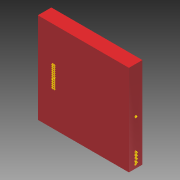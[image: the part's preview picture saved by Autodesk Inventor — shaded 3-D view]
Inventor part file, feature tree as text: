
AUTODESK INVENTOR PART (.ipt)
format: ipt  version: 2011 SP1 (Build 150282100, 282)  size: 317,440 bytes
history: native  units: in
note: dims shown in document units (in); Inventor stores cm internally (conversion verified against a paired STEP export)
features: sketch x14, extrude x4
ambient origin geometry x8: Origin, YZ Plane, XZ Plane, XY Plane, X Axis, Y Axis, Z Axis, Center Point
bodies: Solid1 (feature_tree)
feature tree (18):
  extrude  "Extrusion1"  Depth=3.37in
  extrude  "Extrusion2"  Depth=1.25in
  extrude  "Extrusion3"  Depth=0.5in
  extrude  "Extrusion4"  Depth=0.01in TaperAngle=0.0deg
  sketch  "Sketch5"  dims[d10=0.01in]
  sketch  "Sketch6"  dims[d11=5.1181in d13=0.0625in d14=0.3937in d16=1.0in]
  sketch  "Sketch7"  dims[d18=0.02in d19=0.0in]
  sketch  "Sketch8"  dims[d20=0.0827in]
  sketch  "Sketch9"  dims[d21=0.0276in]
  sketch  "Sketch10"  dims[d22=0.0197in]
  sketch  "Sketch11"  dims[d23=0.7538in]
  sketch  "Sketch12"  dims[d24=0.04in]
  sketch  "Sketch13"  dims[d25=0.7538in]
  sketch  "Sketch14"  dims[d26=0.125in d27=0.375in d28=0.05in d29=0.1in d30=0.01in d31=0.0in]
  sketch  "Sketch1"  dims[d0=3.35in d1=3.37in]
  sketch  "Sketch2"  dims[d2=0.5in d3=0.0in d4=1.25in]
  sketch  "Sketch3"  dims[d5=1.25in d6=0.5in]
  sketch  "Sketch4"  dims[d7=0.125in d8=0.01in d9=0.0in]
